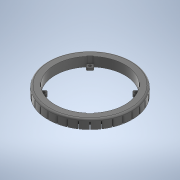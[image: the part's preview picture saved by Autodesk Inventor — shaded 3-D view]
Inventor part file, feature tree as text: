
AUTODESK INVENTOR PART (.ipt)
format: ipt  version: 2020 (Build 240168000, 168)  size: 1,146,880 bytes
history: native  units: mm
features: extrude x9, sketch x8, projected_geometry x8, pattern_circular x5, fillet x4, other x1
ambient origin geometry x8: Origin, YZ Plane, XZ Plane, XY Plane, X Axis, Y Axis, Z Axis, Center Point
bodies: Body1 (feature_tree)
feature tree (35):
  other  "Твердое тело1"
  sketch  "Эскиз1"
  extrude  "Выдавливание1"  Depth=88.0mm
  extrude  "Выдавливание2"  Depth=5.7mm
  pattern_circular  "Круговой массив1"  [2 undecoded]
  extrude  "Выдавливание3"  Depth=5.4mm
  fillet  "Сопряжение1"  Radius=98.0mm
  extrude  "Выдавливание4"  Depth=84.0mm
  pattern_circular  "Круговой массив2"  [2 undecoded]
  fillet  "Сопряжение2"  Radius=98.0mm
  extrude  "Выдавливание5"  Depth=84.0mm
  pattern_circular  "Круговой массив3"  [2 undecoded]
  extrude  "Выдавливание6"  Depth=10.0mm TaperAngle=0.0deg
  fillet  "Сопряжение3"  Radius=320.0mm
  sketch  "Эскиз6"
  extrude  "Выдавливание7"  Depth=2.0mm
  pattern_circular  "Круговой массив4"  [2 undecoded]
  extrude  "Выдавливание8"  Depth=1.0mm TaperAngle=0.0deg
  extrude  "Выдавливание9"  Depth=2.0mm
  pattern_circular  "Круговой массив5"  [2 undecoded]
  fillet  "Сопряжение4"  Radius=320.0mm
  sketch  "Эскиз2"
  sketch  "Эскиз3"
  projected_geometry  "Спроецированная петля1"
  sketch  "Эскиз4"
  projected_geometry  "Спроецированная петля2"
  sketch  "Эскиз5"
  projected_geometry  "Спроецированная петля3"
  projected_geometry  "Спроецированная петля4"
  projected_geometry  "Спроецированная петля5"
  projected_geometry  "Спроецированная петля6"
  projected_geometry  "Спроецированная петля7"
  sketch  "Эскиз7"
  sketch  "Эскиз8"
  projected_geometry  "Спроецированная петля8"
note: 10 required parameter values undecoded (feature->parameter linkage not recoverable at this tier; creation-order binding heuristic only, values carry confidence <= 0.55)
